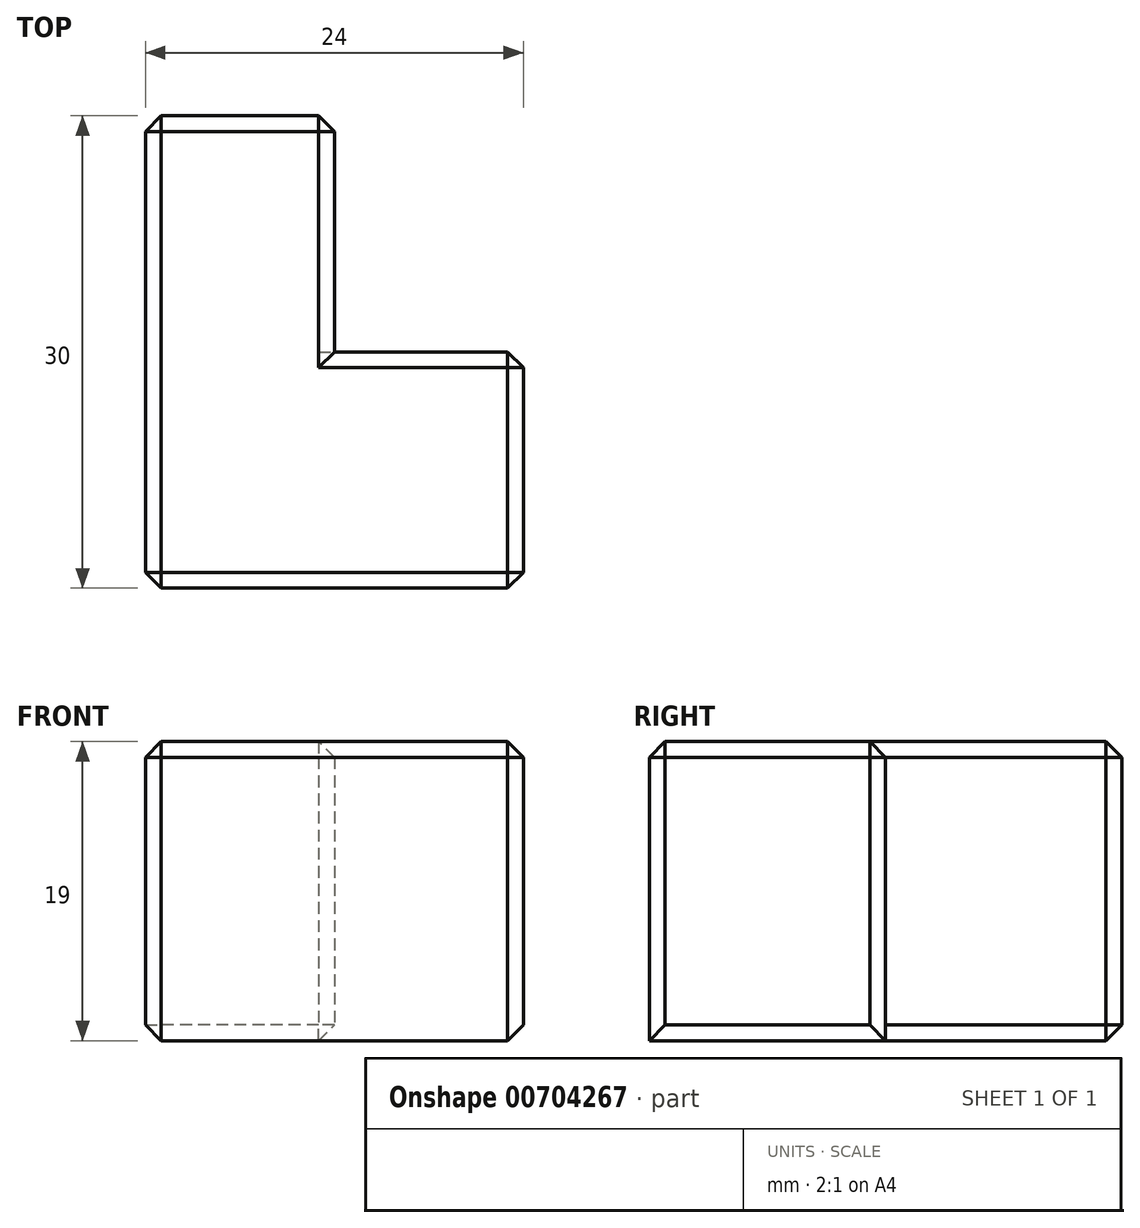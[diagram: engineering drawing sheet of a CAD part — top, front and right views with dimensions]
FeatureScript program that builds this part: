
annotation { "Feature Type Name" : "Feature", "Feature Type Description" : "" }
export const myFeature = defineFeature(function(context is Context, id is Id, definition is map)
    precondition{}
    {
        {
            var Q0;
            Q0=qCreatedBy(makeId("Top.planeOp"),FACE);
            var sketch = newSketch(context, id + "F0", { "sketchPlane" : qUnion([Q0])});
            skLineSegment(sketch, "E0", {"start": v(-12, 15) * mm, "end": v(-12, -15) * mm});
            skLineSegment(sketch, "E1", {"start": v(-12, -15) * mm, "end": v(12, -15) * mm});
            skLineSegment(sketch, "E2", {"start": v(12, -15) * mm, "end": v(12, 0) * mm});
            skLineSegment(sketch, "E3", {"start": v(12, 0) * mm, "end": v(0, 0) * mm});
            skLineSegment(sketch, "E4", {"start": v(-12, 15) * mm, "end": v(0, 15) * mm});
            skLineSegment(sketch, "E5", {"start": v(0, 15) * mm, "end": v(0, 0) * mm});
            skSolve(sketch);
        }
        {
            var Q0;
            Q0=makeQuery(id+"F0.imprint","IMPRINT",FACE,{"disambiguationData":[TD([[makeQuery(id+"F0.imprint","IMPRINT",EDGE,{"derivedFrom":sQuery(id+"F0.wireOp",EDGE,"E0")}),1.0]])]});
            extrude(context, id + "F1", {"entities" : qUnion([Q0]), "depth" : 19 * mm, "offsetDistance" : 25 * mm});
        }
        {
            var Q0;
            Q0=makeQuery(id+"F1.opExtrude","SWEPT_EDGE",EDGE,{"disambiguationData":[OSD([sQuery(id+"F0.wireOp",EDGE,"E4"),sQuery(id+"F0.wireOp",EDGE,"E5")])]});
            var Q1;
            Q1=makeQuery(id+"F1.opExtrude","CAP_FACE",FACE,{"disambiguationData":[OSD([sQuery(id+"F0.wireOp",EDGE,"E0"),sQuery(id+"F0.wireOp",EDGE,"E1"),sQuery(id+"F0.wireOp",EDGE,"E2"),sQuery(id+"F0.wireOp",EDGE,"E3"),sQuery(id+"F0.wireOp",EDGE,"E4"),sQuery(id+"F0.wireOp",EDGE,"E5")])],"isStart":false});
            var Q2;
            Q2=makeQuery(id+"F1.opExtrude","SWEPT_FACE",FACE,{"disambiguationData":[OSD([sQuery(id+"F0.wireOp",EDGE,"E2")])]});
            var Q3;
            Q3=makeQuery(id+"F1.opExtrude","CAP_EDGE",EDGE,{"disambiguationData":[OSD([sQuery(id+"F0.wireOp",EDGE,"E5")])],"isStart":true});
            var Q4;
            Q4=makeQuery(id+"F1.opExtrude","CAP_EDGE",EDGE,{"disambiguationData":[OSD([sQuery(id+"F0.wireOp",EDGE,"E4")])],"isStart":true});
            var Q5;
            Q5=makeQuery(id+"F1.opExtrude","SWEPT_FACE",FACE,{"disambiguationData":[OSD([sQuery(id+"F0.wireOp",EDGE,"E0")])]});
            chamfer(context, id + "F2", {"entities" : qUnion([Q0, Q1, Q2, Q3, Q4, Q5]), "width" : 1 * mm, "tangentPropagation" : true});
        }
    });
